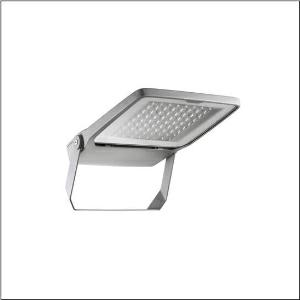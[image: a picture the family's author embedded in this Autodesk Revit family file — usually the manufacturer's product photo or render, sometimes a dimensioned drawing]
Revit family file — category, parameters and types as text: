
# Revit family: floodlight_fl_20_mini___rs17_5xa7672b1b1ac_e4c6
name_source: partatom
category: Lighting Fixtures
units: mm (PartAtom-declared; Revit-internal decimal feet)

## family parameters
Cut with Voids When Loaded = No
Host = Face
Light Source = No
Part Type = Normal
Room Calculation Point = No
Round Connector Dimension = Use Diameter
Shared = No

## types (1)
- --- (1 x LED 3000K / CRI = 80 (unbekannt), 5350 lm, 3000K)
    Apparent Load = 51 VA
    CIE Flux Codes = 79 92 99 100 100
    Color Rendering = 80
    Color Temperature = 3000K
    Default Elevation = 1800 mm
    Description = Floodlight FL 20 mini, floodlight, primary light control with lens, of plastic, primary optical cover: protective disc, of toughened safety glass, transparent, light distribution: RS17, light emission: direct distribution, primary light characteristic: rotationally symmetric, installation type: surface-mounted, LED, High Power LED, rated luminous flux: 5.350lm, luminous efficacy: 105lm/W, light colour: 830, colour temperature: 3000K, control gear: ECG Plus, control: flexible luminous flux parameterisation, time-dependent luminous flux control, digital communication interface, power reduction, overheat protection, electronic power reduction, with terminal, 5-pole, max. 2.5mm², mains connection: 220..240V, AC, 50/60Hz, rated input power: 51W, LED unit, of diecast aluminium, powder-coated, Siteco® metallic grey (DB 702S), corrosivity category C5 mid according to DIN EN ISO 12944, incl. 1x M20 cable gland for cable Ø 6.5..12mm, length: 446mm, width: 355mm, height: 62mm, housing frame, of diecast aluminium, powder-coated, Siteco® metallic grey (DB 702S), mounting bracket, of steel, powder-coated, Siteco® metallic grey (DB 702S), DALI, protection rating (complete): IP66, insulation class (complete): insulation class II (safety insulation), certification: CE, ENEC, VDE, protection symbol: D, permissible operating ambient temperature: -40..+40°C, permissible operating ambient temperature for outdoor applications: -40..+50°C, standard: DIN EN 12944, packaging unit: 1 piece

Light Distribution: RS17
    Height = 62 mm  [stored 0.203412 ft]
    Lamp = 1 x LED 3000K / CRI >= 80 (unbekannt)
    Lamp Light Flux = 5350 lm
    Lamp count = 1
    Length = 467 mm
    Luminous efficacy = 105 lm/W
    Manufacturer = Siteco
    ModVariant = No
    Model = 5XA7672B1B1AC
    Mounting Place = Wall
    Mounting Type = Surface mounted
    Number of Poles = 1
    OnlyDefault = Yes
    Power Factor = 1
    Product Name = Floodlight FL 20 mini | RS17
    Product group = floodlight | wall mounted
    ProductGroupID = 2001
    Protection Class = Protection class II
    Protection Degree = IP 66
    RLX_Detail_Level = 1
    RLX_Emergency_Light_Flux = 0 lm
    RLX_Emergency_Type = 0
    RLX_Emergency_Type_DB = No
    RlxData = <blob elided: 68897 chars, md5=b3aa87c9>
    Socket = socket
    Standby Power = 0 W
    System Light Flux = 5350 lm
    System Power = 51 W
    Type Comments = factory setting: luminous flux: 100 % | dim-lin: 254 | 520 mA
    Type Image = l_1005948.jpg
    URL = http://relux.com
    VarID = @adj_163121
    Voltage = 0 V
    Weight = 0.00 kg
    Width = 335 mm

note: [stored X ft] marks values corroborated as IEEE doubles in the binary element streams (Revit-internal decimal feet)

## geometry (parser evidence)
native form markers: Blend x4, Sweep x12
no freeform markers — native parametric forms only
